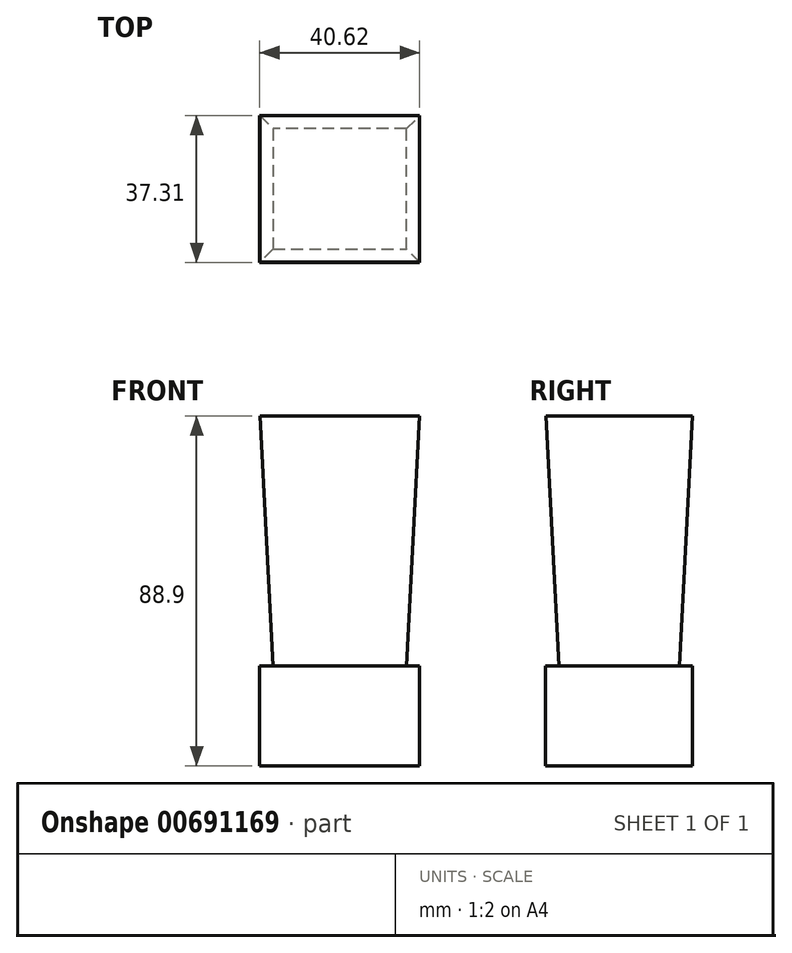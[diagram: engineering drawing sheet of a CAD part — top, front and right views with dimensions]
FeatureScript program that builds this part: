
annotation { "Feature Type Name" : "Feature", "Feature Type Description" : "" }
export const myFeature = defineFeature(function(context is Context, id is Id, definition is map)
    precondition{}
    {
        {
            var Q0;
            Q0=qCreatedBy(makeId("Top.planeOp"),FACE);
            var sketch = newSketch(context, id + "F0", { "sketchPlane" : qUnion([Q0])});
            skLineSegment(sketch, "E0.bottom", {"start": v(0, 0) * mm, "end": v(31.24, 0) * mm});
            skLineSegment(sketch, "E0.top", {"start": v(0, 27.94) * mm, "end": v(31.24, 27.94) * mm});
            skLineSegment(sketch, "E0.left", {"start": v(0, 0) * mm, "end": v(0, 27.94) * mm});
            skLineSegment(sketch, "E0.right", {"start": v(31.24, 0) * mm, "end": v(31.24, 27.94) * mm});
            skSolve(sketch);
        }
        {
            var Q0;
            Q0=makeQuery(id+"F0.imprint","IMPRINT",FACE,{"disambiguationData":[TD([[makeQuery(id+"F0.imprint","IMPRINT",EDGE,{"derivedFrom":sQuery(id+"F0.wireOp",EDGE,"E0.bottom")}),1.0]])]});
            extrude(context, id + "F1", {"entities" : qUnion([Q0]), "depth" : 88.9 * mm, "offsetDistance" : 25.4 * mm, "hasDraft" : true, "draftAngle" : 3 * degree});
        }
        {
            var Q0;
            Q0=makeQuery(id+"F1.opExtrude","CAP_FACE",FACE,{"disambiguationData":[OSD([sQuery(id+"F0.wireOp",EDGE,"E0.bottom"),sQuery(id+"F0.wireOp",EDGE,"E0.top"),sQuery(id+"F0.wireOp",EDGE,"E0.left"),sQuery(id+"F0.wireOp",EDGE,"E0.right")])],"isStart":true});
            var sketch = newSketch(context, id + "F2", { "sketchPlane" : qUnion([Q0])});
            skLineSegment(sketch, "E1.bottom", {"start": v(-4.72, 4.71) * mm, "end": v(35.9, 4.71) * mm});
            skLineSegment(sketch, "E1.top", {"start": v(-4.72, -32.6) * mm, "end": v(35.9, -32.6) * mm});
            skLineSegment(sketch, "E1.left", {"start": v(-4.72, 4.71) * mm, "end": v(-4.72, -32.6) * mm});
            skLineSegment(sketch, "E1.right", {"start": v(35.9, 4.71) * mm, "end": v(35.9, -32.6) * mm});
            skSolve(sketch);
        }
        {
            var Q0;
            Q0 = qSketchRegion(id + "F2", true);
            extrude(context, id + "F3", {"entities" : qUnion([Q0]), "operationType" : NewBodyOperationType.ADD, "oppositeDirection" : true, "depth" : 25.4 * mm, "offsetDistance" : 25.4 * mm});
        }
    });
